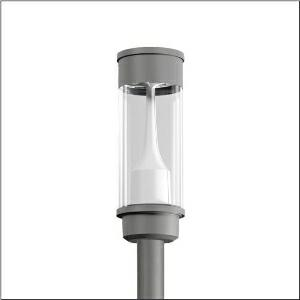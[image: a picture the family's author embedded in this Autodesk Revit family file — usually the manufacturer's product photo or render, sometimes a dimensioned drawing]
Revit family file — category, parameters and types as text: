
# Revit family: litepole_iq___pl1_2s_5xa5415of14h_b306
name_source: partatom
category: Lighting Fixtures
units: mm (PartAtom-declared; Revit-internal decimal feet)

## family parameters
Cut with Voids When Loaded = No
Host = Face
Light Source = No
Part Type = Normal
Room Calculation Point = No
Round Connector Dimension = Use Diameter
Shared = No

## types (1)
- --- (1 x LED, 2970 lm, 21.8 W, 2700K)
    Apparent Load = 22 VA
    CIE Flux Codes = 23 62 94 96 100
    Color Rendering = 70
    Color Temperature = 2700K
    Default Elevation = 1800 mm
    Description = Litepole iQ, mast luminaire, Module 540 iQ-SR, primary light control with 3 zone facetted reflector, of plastic, silver coated, highly specular, structured, primary optical cover: cover, of PMMA, transparent, partly coated, light distribution: PL1.2s, light emission: direct distribution, primary light characteristic: symmetric, installation type: post-top, LED, High Power LED, rated luminous flux: 2.970lm, luminous efficacy: 136lm/W, light colour: 727, colour temperature: 2700K, control gear: iQ Street-Remote, control: optimised constant luminous flux control (CLO 2.0), Desk-Remote (wireless, voltage-free reading and setting of iQ features in the workshop via application-optimized NFC function/RFID function), Light-Fading, Smart-Wire, Night-Set, Lumen-Switch, Temp-Guard, Auto-Match, Street-Remote, pre-setting: logarithmic dimming characteristic, with terminal, 6-pole, max. 2.5mm², mains connection: 230..240V, AC, 50/60Hz, start of lifetime: 22W, end of service life: 23W, reduction: 11W, luminaire housing, upper part, of glass-fibre reinforced polyester, coated, Siteco® metallic grey (DB 702S), diameter: 210mm, height: 590mm, spigot size: d x l = 76 x 70mm (post-top) | with reducer (optional accessory) 60 x 70mm, mounting height: 3..5m, post-top mast mounting element, of diecast aluminium, coated, Siteco® metallic grey (DB 702S), Module 540 iQ-SR, traffic white (RAL 9016), equipment: standard, protection rating (complete): IP65, insulation class (complete): insulation class II (safety insulation), certification: CE, ENEC, VDE, packaging unit: 1 piece

Light Distribution: PL1.2s
    Height = 590 mm
    Lamp = 1 x LED
    Lamp Light Flux = 2970 lm
    Lamp Power = 21.8 W
    Lamp count = 1
    Length = 220 mm
    Luminous efficacy = 136 lm/W
    Manufacturer = Siteco
    ModVariant = No
    Model = 5XA5415OF14H
    Number of Poles = 1
    OnlyDefault = Yes
    Power Factor = 1
    Product Name = Litepole iQ | PL1.2s
    Product group = mast luminaire | pylon top
    ProductGroupID = 6100
    Protection Class = Protection class II
    Protection Degree = IP 65
    RLX_Detail_Level = 1
    RLX_Emergency_Light_Flux = 0 lm
    RLX_Emergency_Type = 0
    RLX_Emergency_Type_DB = No
    RlxData = <blob elided: 24981 chars, md5=89d4a3f2>
    Socket = socket
    Standby Power = 0 W
    System Light Flux = 2970 lm
    System Power = 22 W
    Type Comments = factory setting: luminous flux: 100 % | dim-lin: 254 | 456 mA
    Type Image = l_1006025.jpg
    URL = http://relux.com
    VarID = @adj_166199
    Voltage = 0 V
    Weight = 0.00 kg
    Width = 0 mm  [stored 0 ft]

note: [stored X ft] marks values corroborated as IEEE doubles in the binary element streams (Revit-internal decimal feet)

## geometry (parser evidence)
native form markers: Blend x4, Sweep x12
no freeform markers — native parametric forms only
